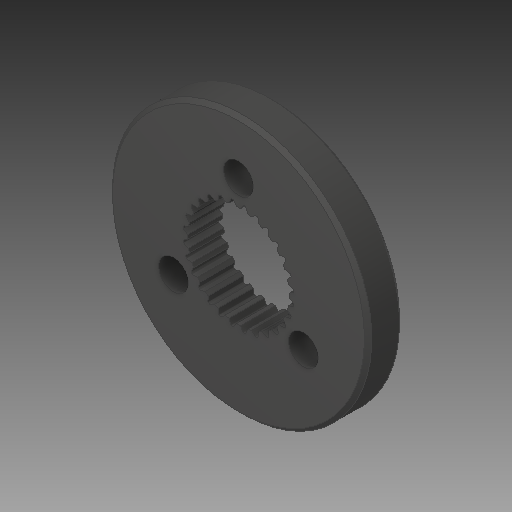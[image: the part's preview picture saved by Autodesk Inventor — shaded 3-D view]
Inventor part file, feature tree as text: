
AUTODESK INVENTOR PART (.ipt)
format: ipt  version: 2018 (Build 220112000, 112)  size: 275,968 bytes
history: native  units: in
note: dims shown in document units (in); Inventor stores cm internally (conversion verified against a paired STEP export)
features: chamfer x1
ambient origin geometry x8: Origin, YZ Plane, XZ Plane, XY Plane, X Axis, Y Axis, Z Axis, Center Point
bodies: Solid1 (feature_tree)
feature tree (1):
  chamfer  "Chamfer1"  [1 undecoded]
note: 1 required parameter value undecoded (feature->parameter linkage not recoverable at this tier; creation-order binding heuristic only, values carry confidence <= 0.55)
